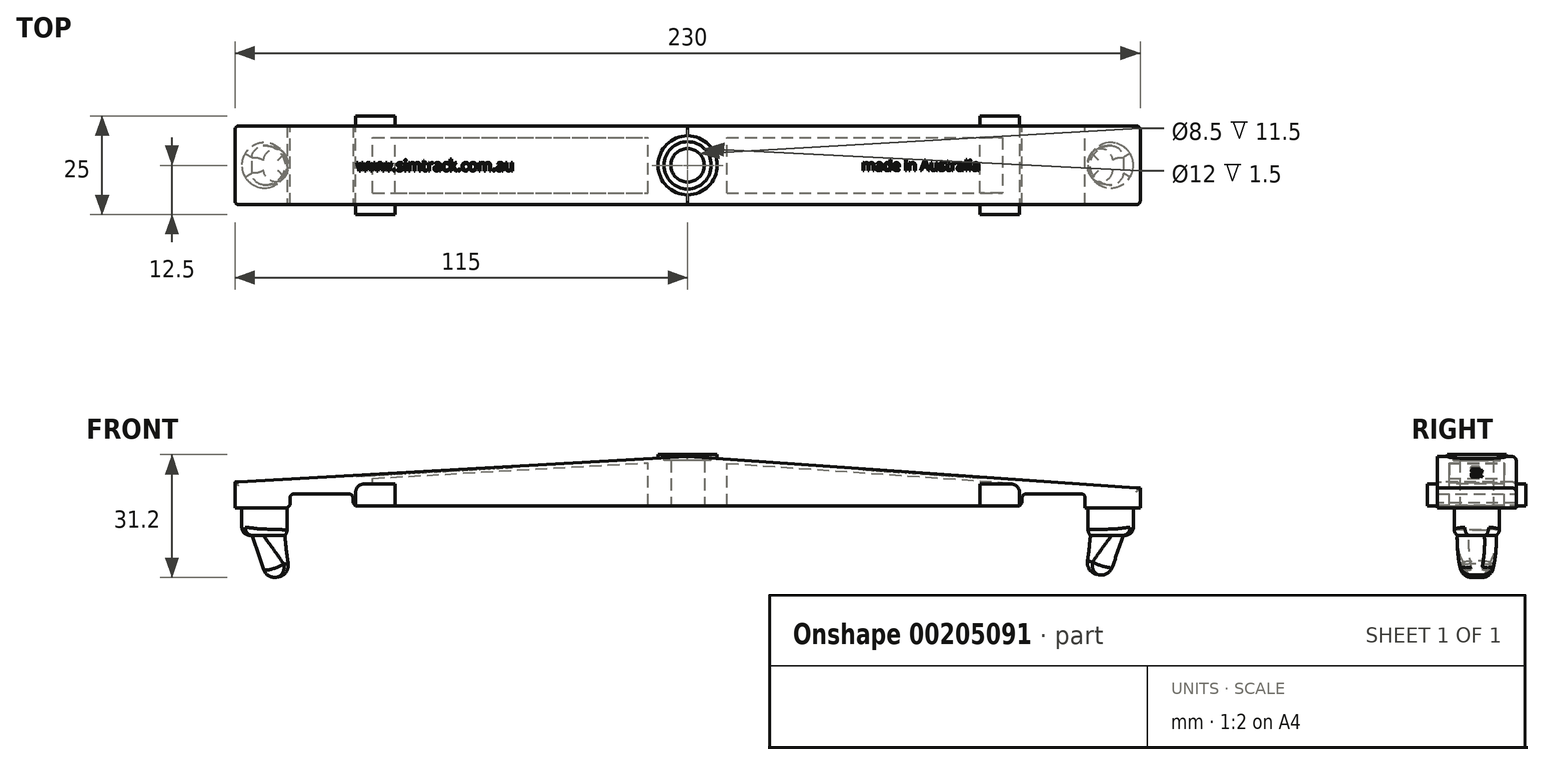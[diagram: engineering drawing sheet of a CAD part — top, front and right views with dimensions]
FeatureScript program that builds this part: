
annotation { "Feature Type Name" : "Feature", "Feature Type Description" : "" }
export const myFeature = defineFeature(function(context is Context, id is Id, definition is map)
    precondition{}
    {
        {
            var Q0;
            Q0=qCreatedBy(makeId("Top.planeOp"),FACE);
            var sketch = newSketch(context, id + "F0", { "sketchPlane" : qUnion([Q0])});
            skCircle(sketch, "E0", {"center": v(0, 0) * mm, "radius": 4.25 * mm});
            skLineSegment(sketch, "E1.bottom", {"start": v(115, -10) * mm, "end": v(-115, -10) * mm});
            skLineSegment(sketch, "E1.top", {"start": v(115, 10) * mm, "end": v(-115, 10) * mm});
            skLineSegment(sketch, "E1.left", {"start": v(115, -10) * mm, "end": v(115, 10) * mm});
            skLineSegment(sketch, "E1.right", {"start": v(-115, -10) * mm, "end": v(-115, 10) * mm});
            skPoint(sketch, "E2.visualSharp", {"position": v(-115, 10) * mm});
            skLineSegment(sketch, "E2.filletArc", {"start": v(-115, 10) * mm, "end": v(-115, 10) * mm});
            skPoint(sketch, "E3.visualSharp", {"position": v(-115, -10) * mm});
            skLineSegment(sketch, "E3.filletArc", {"start": v(-115, -10) * mm, "end": v(-115, -10) * mm});
            skPoint(sketch, "E4.visualSharp", {"position": v(115, 10) * mm});
            skLineSegment(sketch, "E4.filletArc", {"start": v(115, 10) * mm, "end": v(115, 10) * mm});
            skPoint(sketch, "E5.visualSharp", {"position": v(115, -10) * mm});
            skLineSegment(sketch, "E5.filletArc", {"start": v(115, -10) * mm, "end": v(115, -10) * mm});
            skLineSegment(sketch, "E6.bottom", {"start": v(80, 7) * mm, "end": v(10, 7) * mm});
            skLineSegment(sketch, "E6.top", {"start": v(80, -7) * mm, "end": v(10, -7) * mm});
            skLineSegment(sketch, "E6.left", {"start": v(80, 7) * mm, "end": v(80, -7) * mm});
            skLineSegment(sketch, "E6.right", {"start": v(10, 7) * mm, "end": v(10, -7) * mm});
            skLineSegment(sketch, "E7.bottom", {"start": v(-10, 7) * mm, "end": v(-80, 7) * mm});
            skLineSegment(sketch, "E7.top", {"start": v(-10, -7) * mm, "end": v(-80, -7) * mm});
            skLineSegment(sketch, "E7.left", {"start": v(-10, 7) * mm, "end": v(-10, -7) * mm});
            skLineSegment(sketch, "E7.right", {"start": v(-80, 7) * mm, "end": v(-80, -7) * mm});
            skCircle(sketch, "E8", {"center": v(0, 0) * mm, "radius": 7.5 * mm});
            skSolve(sketch);
        }
        {
            var Q0;
            Q0=makeQuery(id+"F0.imprint","IMPRINT",FACE,{"disambiguationData":[TD([[makeQuery(id+"F0.imprint","IMPRINT",EDGE,{"derivedFrom":sQuery(id+"F0.wireOp",EDGE,"E1.bottom")}),-1.0]])]});
            var Q1;
            Q1=makeQuery(id+"F0.imprint","IMPRINT",FACE,{"disambiguationData":[TD([[makeQuery(id+"F0.imprint","IMPRINT",EDGE,{"derivedFrom":sQuery(id+"F0.wireOp",EDGE,"q9BRd2um-oMs7-7MK2-WjCr-aT8UQEt5jsp8")}),-1.0]])]});
            var Q2;
            {var subQ0=sQuery(id+"F0.wireOp",EDGE,"CfEYtvD2-7vdv-HU4w-jJwD-IvnwvT9jjSvh.right");var subQ1=sQuery(id+"F0.wireOp",EDGE,"TnjMtal5-3gMc-DNrO-T4Mg-M14iXYZFMKTD");var subQ2=makeQuery(id+"F0.imprint","INTERSECT",VERTEX,{"disambiguationData":[OD(0.0)],"derivedFrom":[subQ1,subQ0]});Q2=makeQuery(id+"F0.imprint","IMPRINT",FACE,{"disambiguationData":[TD([[makeQuery(id+"F0.imprint","IMPRINT",EDGE,{"disambiguationData":[TD([[subQ2,1.0]])],"derivedFrom":subQ1}),1.0]])]});}
            var Q3;
            {var subQ0=sQuery(id+"F0.wireOp",EDGE,"CfEYtvD2-7vdv-HU4w-jJwD-IvnwvT9jjSvh.left");var subQ1=sQuery(id+"F0.wireOp",EDGE,"O0jPoW7s-RU5z-iA6U-w5ju-wIfl1B3ZVbkh");var subQ2=makeQuery(id+"F0.imprint","INTERSECT",VERTEX,{"disambiguationData":[OD(0.0)],"derivedFrom":[subQ1,subQ0]});Q3=makeQuery(id+"F0.imprint","IMPRINT",FACE,{"disambiguationData":[TD([[makeQuery(id+"F0.imprint","IMPRINT",EDGE,{"disambiguationData":[TD([[subQ2,-1.0]])],"derivedFrom":subQ1}),1.0]])]});}
            var Q4;
            {var subQ0=sQuery(id+"F0.wireOp",EDGE,"CfEYtvD2-7vdv-HU4w-jJwD-IvnwvT9jjSvh.right");var subQ1=sQuery(id+"F0.wireOp",EDGE,"TnjMtal5-3gMc-DNrO-T4Mg-M14iXYZFMKTD");var subQ2=makeQuery(id+"F0.imprint","INTERSECT",VERTEX,{"disambiguationData":[OD(0.0)],"derivedFrom":[subQ1,subQ0]});Q4=makeQuery(id+"F0.imprint","IMPRINT",FACE,{"disambiguationData":[TD([[makeQuery(id+"F0.imprint","IMPRINT",EDGE,{"disambiguationData":[TD([[subQ2,-1.0]])],"derivedFrom":subQ1}),1.0]])]});}
            var Q5;
            {var subQ0=sQuery(id+"F0.wireOp",EDGE,"CfEYtvD2-7vdv-HU4w-jJwD-IvnwvT9jjSvh.left");var subQ1=sQuery(id+"F0.wireOp",EDGE,"O0jPoW7s-RU5z-iA6U-w5ju-wIfl1B3ZVbkh");var subQ2=makeQuery(id+"F0.imprint","INTERSECT",VERTEX,{"disambiguationData":[OD(0.0)],"derivedFrom":[subQ1,subQ0]});Q5=makeQuery(id+"F0.imprint","IMPRINT",FACE,{"disambiguationData":[TD([[makeQuery(id+"F0.imprint","IMPRINT",EDGE,{"disambiguationData":[TD([[subQ2,1.0]])],"derivedFrom":subQ1}),1.0]])]});}
            extrude(context, id + "F1", {"entities" : qUnion([Q0, Q1, Q2, Q3, Q4, Q5]), "oppositeDirection" : true, "depth" : 5 * mm, "hasSecondDirection" : true, "secondDirectionOppositeDirection" : false, "secondDirectionDepth" : 8 * mm});
        }
        {
            var Q0;
            Q0=makeQuery(id+"F1.opExtrude","SWEPT_FACE",FACE,{"disambiguationData":[OSD([sQuery(id+"F0.wireOp",EDGE,"E1.bottom")])]});
            var sketch = newSketch(context, id + "F2", { "sketchPlane" : qUnion([Q0])});
            skLineSegment(sketch, "E9", {"start": v(-115, 1.5) * mm, "end": v(0, 8) * mm});
            skLineSegment(sketch, "E10", {"start": v(0, 8) * mm, "end": v(115, 0) * mm});
            skSolve(sketch);
        }
        {
            var Q0;
            {var subQ0=sQuery(id+"F2.wireOp",EDGE,"E10");Q0=makeQuery(id+"F2.imprint","IMPRINT",FACE,{"disambiguationData":[TD([[makeQuery(id+"F2.imprint","IMPRINT",EDGE,{"derivedFrom":subQ0}),1.0]])]});}
            var Q1;
            {var subQ0=sQuery(id+"F2.wireOp",EDGE,"E9");Q1=makeQuery(id+"F2.imprint","IMPRINT",FACE,{"disambiguationData":[TD([[makeQuery(id+"F2.imprint","IMPRINT",EDGE,{"derivedFrom":subQ0}),1.0]])]});}
            extrude(context, id + "F3", {"entities" : qUnion([Q0, Q1]), "operationType" : NewBodyOperationType.REMOVE, "oppositeDirection" : true, "depth" : 25 * mm});
        }
        {
            var Q0;
            Q0=makeQuery(id+"F0.imprint","IMPRINT",FACE,{"disambiguationData":[TD([[makeQuery(id+"F0.imprint","IMPRINT",EDGE,{"derivedFrom":sQuery(id+"F0.wireOp",EDGE,"E0")}),-1.0]])]});
            var Q1;
            Q1=makeQuery(id+"F0.imprint","IMPRINT",FACE,{"disambiguationData":[TD([[makeQuery(id+"F0.imprint","IMPRINT",EDGE,{"derivedFrom":sQuery(id+"F0.wireOp",EDGE,"E0")}),1.0]])]});
            extrude(context, id + "F4", {"entities" : qUnion([Q0, Q1]), "operationType" : NewBodyOperationType.ADD, "oppositeDirection" : true, "depth" : 5 * mm});
        }
        {
            var Q0;
            Q0=makeQuery(id+"F0.imprint","IMPRINT",FACE,{"disambiguationData":[TD([[makeQuery(id+"F0.imprint","IMPRINT",EDGE,{"derivedFrom":sQuery(id+"F0.wireOp",EDGE,"E0")}),1.0]])]});
            extrude(context, id + "F5", {"entities" : qUnion([Q0]), "operationType" : NewBodyOperationType.REMOVE, "depth" : 8 * mm, "hasSecondDirection" : true, "secondDirectionOppositeDirection" : true, "secondDirectionDepth" : 5 * mm});
        }
        {
            var Q0;
            Q0=makeQuery(id+"F1.opExtrude","SWEPT_FACE",FACE,{"disambiguationData":[OSD([sQuery(id+"F0.wireOp",EDGE,"E1.bottom")])]});
            var sketch = newSketch(context, id + "F6", { "sketchPlane" : qUnion([Q0])});
            skSolve(sketch);
        }
        {
            var Q0;
            Q0=makeQuery(id+"F1.opExtrude","SWEPT_FACE",FACE,{"disambiguationData":[OSD([sQuery(id+"F0.wireOp",EDGE,"E1.top")])]});
            var sketch = newSketch(context, id + "F7", { "sketchPlane" : qUnion([Q0])});
            skLineSegment(sketch, "E11", {"start": v(-115, -5) * mm, "end": v(-101, -5) * mm});
            skLineSegment(sketch, "E12", {"start": v(-101, -5) * mm, "end": v(-101, -1.5) * mm});
            skLineSegment(sketch, "E13", {"start": v(-101, -1.5) * mm, "end": v(-85, -1.5) * mm});
            skLineSegment(sketch, "E14", {"start": v(-85, -1.5) * mm, "end": v(-85, -5) * mm});
            skLineSegment(sketch, "E15", {"start": v(-85, -5) * mm, "end": v(-101, -5) * mm});
            skLineSegment(sketch, "E16", {"start": v(115, -5) * mm, "end": v(101, -5) * mm});
            skLineSegment(sketch, "E17", {"start": v(101, -5) * mm, "end": v(101, -1.5) * mm});
            skLineSegment(sketch, "E18", {"start": v(101, -1.5) * mm, "end": v(85, -1.5) * mm});
            skLineSegment(sketch, "E19", {"start": v(85, -1.5) * mm, "end": v(85, -5) * mm});
            skLineSegment(sketch, "E20", {"start": v(85, -5) * mm, "end": v(101, -5) * mm});
            skSolve(sketch);
        }
        {
            var Q0;
            Q0=makeQuery(id+"F7.imprint","IMPRINT",FACE,{"disambiguationData":[TD([[makeQuery(id+"F7.imprint","IMPRINT",EDGE,{"derivedFrom":sQuery(id+"F7.wireOp",EDGE,"E12")}),-1.0]])]});
            var Q1;
            Q1=makeQuery(id+"F7.imprint","IMPRINT",FACE,{"disambiguationData":[TD([[makeQuery(id+"F7.imprint","IMPRINT",EDGE,{"derivedFrom":sQuery(id+"F7.wireOp",EDGE,"E17")}),1.0]])]});
            extrude(context, id + "F8", {"entities" : qUnion([Q0, Q1]), "operationType" : NewBodyOperationType.REMOVE, "oppositeDirection" : true, "depth" : 25 * mm});
        }
        {
            var Q0;
            Q0=makeQuery(id+"F3.boolean.opBoolean","COPY",FACE,{"derivedFrom":makeQuery(id+"F3.opExtrude","SWEPT_FACE",FACE,{"disambiguationData":[OSD([sQuery(id+"F2.wireOp",EDGE,"E9")])]})});
            var sketch = newSketch(context, id + "F9", { "sketchPlane" : qUnion([Q0])});
            skCircle(sketch, "E21", {"center": v(-107.72, 0) * mm, "radius": 5 * mm});
            skSolve(sketch);
        }
        {
            var Q0;
            Q0=makeQuery(id+"F9.imprint","IMPRINT",FACE,{"disambiguationData":[TD([[makeQuery(id+"F9.imprint","IMPRINT",EDGE,{"derivedFrom":sQuery(id+"F9.wireOp",EDGE,"E21")}),1.0]])]});
            extrude(context, id + "F10", {"entities" : qUnion([Q0]), "operationType" : NewBodyOperationType.ADD, "oppositeDirection" : true, "depth" : 8 * mm});
        }
        {
            var Q0;
            Q0=makeQuery(id+"F3.boolean.opBoolean","COPY",FACE,{"derivedFrom":makeQuery(id+"F3.opExtrude","SWEPT_FACE",FACE,{"disambiguationData":[OSD([sQuery(id+"F2.wireOp",EDGE,"E10")])]})});
            var sketch = newSketch(context, id + "F11", { "sketchPlane" : qUnion([Q0])});
            skCircle(sketch, "E22", {"center": v(107.7, 0) * mm, "radius": 5 * mm});
            skSolve(sketch);
        }
        {
            var Q0;
            Q0=makeQuery(id+"F11.imprint","IMPRINT",FACE,{"disambiguationData":[TD([[makeQuery(id+"F11.imprint","IMPRINT",EDGE,{"derivedFrom":sQuery(id+"F11.wireOp",EDGE,"E22")}),1.0]])]});
            extrude(context, id + "F12", {"entities" : qUnion([Q0]), "operationType" : NewBodyOperationType.ADD, "oppositeDirection" : true, "depth" : 6 * mm});
        }
        {
            var Q0;
            Q0=makeQuery(id+"F0.imprint","IMPRINT",FACE,{"disambiguationData":[TD([[makeQuery(id+"F0.imprint","IMPRINT",EDGE,{"derivedFrom":sQuery(id+"F0.wireOp",EDGE,"E7.bottom")}),1.0]])]});
            var Q1;
            Q1=makeQuery(id+"F0.imprint","IMPRINT",FACE,{"disambiguationData":[TD([[makeQuery(id+"F0.imprint","IMPRINT",EDGE,{"derivedFrom":sQuery(id+"F0.wireOp",EDGE,"E6.bottom")}),1.0]])]});
            extrude(context, id + "F13", {"entities" : qUnion([Q0, Q1]), "operationType" : NewBodyOperationType.REMOVE, "depth" : 29 * mm, "hasDraft" : true, "draftAngle" : 3 * degree});
        }
        {
            var Q0;
            {var subQ0=sQuery(id+"F0.wireOp",EDGE,"E1.bottom");Q0=makeQuery(id+"F6.imprint","IMPRINT",FACE,{"disambiguationData":[TD([[makeQuery(id+"F6.imprint","IMPRINT",EDGE,{"derivedFrom":makeQuery(id+"F1.opExtrude","CAP_EDGE",EDGE,{"disambiguationData":[OSD([subQ0])],"isStart":false})}),-1.0]])]});}
            var sketch = newSketch(context, id + "F14", { "sketchPlane" : qUnion([Q0])});
            skSolve(sketch);
        }
        {
            var Q0;
            Q0=makeQuery(id+"F1.opExtrude","SWEPT_FACE",FACE,{"disambiguationData":[OSD([sQuery(id+"F0.wireOp",EDGE,"E1.top")])]});
            extrude(context, id + "F15", {"entities" : qUnion([Q0]), "operationType" : NewBodyOperationType.ADD, "oppositeDirection" : true, "depth" : 20 * mm});
        }
        {
            var Q0;
            Q0=makeQuery(id+"F0.imprint","IMPRINT",FACE,{"disambiguationData":[TD([[makeQuery(id+"F0.imprint","IMPRINT",EDGE,{"derivedFrom":sQuery(id+"F0.wireOp",EDGE,"E7.bottom")}),1.0]])]});
            var Q1;
            Q1=makeQuery(id+"F0.imprint","IMPRINT",FACE,{"disambiguationData":[TD([[makeQuery(id+"F0.imprint","IMPRINT",EDGE,{"derivedFrom":sQuery(id+"F0.wireOp",EDGE,"E6.bottom")}),1.0]])]});
            extrude(context, id + "F16", {"entities" : qUnion([Q0, Q1]), "operationType" : NewBodyOperationType.REMOVE, "oppositeDirection" : true, "depth" : 25 * mm, "hasSecondDirection" : true, "secondDirectionOppositeDirection" : false, "secondDirectionDepth" : 25 * mm});
        }
        {
            var Q0;
            Q0=makeQuery(id+"F0.imprint","IMPRINT",FACE,{"disambiguationData":[TD([[makeQuery(id+"F0.imprint","IMPRINT",EDGE,{"derivedFrom":sQuery(id+"F0.wireOp",EDGE,"E0")}),-1.0]])]});
            extrude(context, id + "F17", {"entities" : qUnion([Q0]), "operationType" : NewBodyOperationType.ADD, "depth" : 8.5 * mm});
        }
        {
            var Q0;
            Q0=makeQuery(id+"F0.imprint","IMPRINT",FACE,{"disambiguationData":[TD([[makeQuery(id+"F0.imprint","IMPRINT",EDGE,{"derivedFrom":sQuery(id+"F0.wireOp",EDGE,"E0")}),1.0]])]});
            extrude(context, id + "F18", {"entities" : qUnion([Q0]), "operationType" : NewBodyOperationType.REMOVE, "oppositeDirection" : true, "depth" : 25 * mm, "hasSecondDirection" : true, "secondDirectionOppositeDirection" : false, "secondDirectionDepth" : 25 * mm});
        }
        {
            var Q0;
            Q0=makeQuery(id+"F3.boolean.opBoolean","COPY",EDGE,{"derivedFrom":makeQuery(id+"F3.opExtrude","SWEPT_EDGE",EDGE,{"disambiguationData":[OSD([sQuery(id+"F0.wireOp",EDGE,"E1.bottom"),sQuery(id+"F0.wireOp",EDGE,"E1.left"),sQuery(id+"F2.wireOp",EDGE,"E10")])]})});
            var Q1;
            Q1=makeQuery(id+"F3.boolean.opBoolean","INTERSECT",EDGE,{"derivedFrom":[makeQuery(id+"F1.opExtrude","SWEPT_FACE",FACE,{"disambiguationData":[OSD([sQuery(id+"F0.wireOp",EDGE,"E1.top")])]}),makeQuery(id+"F3.opExtrude","SWEPT_FACE",FACE,{"disambiguationData":[OSD([sQuery(id+"F2.wireOp",EDGE,"E10")])]})]});
            var Q2;
            Q2=makeQuery(id+"F3.boolean.opBoolean","INTERSECT",EDGE,{"derivedFrom":[makeQuery(id+"F1.opExtrude","SWEPT_FACE",FACE,{"disambiguationData":[OSD([sQuery(id+"F0.wireOp",EDGE,"E1.top")])]}),makeQuery(id+"F3.opExtrude","SWEPT_FACE",FACE,{"disambiguationData":[OSD([sQuery(id+"F2.wireOp",EDGE,"E9")])]})]});
            var Q3;
            Q3=makeQuery(id+"F3.boolean.opBoolean","COPY",EDGE,{"derivedFrom":makeQuery(id+"F3.opExtrude","SWEPT_EDGE",EDGE,{"disambiguationData":[OSD([sQuery(id+"F0.wireOp",EDGE,"E1.bottom"),sQuery(id+"F0.wireOp",EDGE,"E1.right"),sQuery(id+"F2.wireOp",EDGE,"E9")])]})});
            var Q4;
            Q4=makeQuery(id+"F1.opExtrude","SWEPT_EDGE",EDGE,{"disambiguationData":[OSD([sQuery(id+"F0.wireOp",EDGE,"E1.bottom"),sQuery(id+"F0.wireOp",EDGE,"E1.right")])]});
            var Q5;
            Q5=makeQuery(id+"F1.opExtrude","SWEPT_EDGE",EDGE,{"disambiguationData":[OSD([sQuery(id+"F0.wireOp",EDGE,"E1.top"),sQuery(id+"F0.wireOp",EDGE,"E1.right")])]});
            var Q6;
            Q6=makeQuery(id+"F3.boolean.opBoolean","COPY",EDGE,{"derivedFrom":makeQuery(id+"F3.opExtrude","CAP_EDGE",EDGE,{"disambiguationData":[OSD([sQuery(id+"F2.wireOp",EDGE,"E10")])],"isStart":true})});
            var Q7;
            Q7=makeQuery(id+"F3.boolean.opBoolean","COPY",EDGE,{"derivedFrom":makeQuery(id+"F3.opExtrude","CAP_EDGE",EDGE,{"disambiguationData":[OSD([sQuery(id+"F2.wireOp",EDGE,"E9")])],"isStart":true})});
            var Q8;
            Q8=makeQuery(id+"F1.opExtrude","SWEPT_EDGE",EDGE,{"disambiguationData":[OSD([sQuery(id+"F0.wireOp",EDGE,"E1.top"),sQuery(id+"F0.wireOp",EDGE,"E1.left")])]});
            var Q9;
            Q9=makeQuery(id+"F1.opExtrude","SWEPT_EDGE",EDGE,{"disambiguationData":[OSD([sQuery(id+"F0.wireOp",EDGE,"E1.bottom"),sQuery(id+"F0.wireOp",EDGE,"E1.left")])]});
            fillet(context, id + "F19", {"entities" : qUnion([Q0, Q1, Q2, Q3, Q4, Q5, Q6, Q7, Q8, Q9]), "radius" : 1 * mm, "tangentPropagation" : true, "allowEdgeOverflow" : false});
        }
        {
            var Q0;
            Q0=makeQuery(id+"F8.boolean.opBoolean","COPY",EDGE,{"derivedFrom":makeQuery(id+"F8.opExtrude","SWEPT_EDGE",EDGE,{"disambiguationData":[OSD([sQuery(id+"F7.wireOp",EDGE,"E18"),sQuery(id+"F7.wireOp",EDGE,"E19")])]})});
            var Q1;
            Q1=makeQuery(id+"F8.boolean.opBoolean","COPY",EDGE,{"derivedFrom":makeQuery(id+"F8.opExtrude","SWEPT_EDGE",EDGE,{"disambiguationData":[OSD([sQuery(id+"F7.wireOp",EDGE,"E17"),sQuery(id+"F7.wireOp",EDGE,"E18")])]})});
            var Q2;
            Q2=makeQuery(id+"F8.boolean.opBoolean","COPY",EDGE,{"derivedFrom":makeQuery(id+"F8.opExtrude","SWEPT_EDGE",EDGE,{"disambiguationData":[OSD([sQuery(id+"F7.wireOp",EDGE,"E13"),sQuery(id+"F7.wireOp",EDGE,"E14")])]})});
            var Q3;
            Q3=makeQuery(id+"F8.boolean.opBoolean","COPY",EDGE,{"derivedFrom":makeQuery(id+"F8.opExtrude","SWEPT_EDGE",EDGE,{"disambiguationData":[OSD([sQuery(id+"F7.wireOp",EDGE,"E12"),sQuery(id+"F7.wireOp",EDGE,"E13")])]})});
            fillet(context, id + "F20", {"entities" : qUnion([Q0, Q1, Q2, Q3]), "radius" : 1 * mm, "tangentPropagation" : true, "allowEdgeOverflow" : false});
        }
        {
            var Q0;
            {var subQ1=sQuery(id+"F0.wireOp",EDGE,"E1.top");var subQ2=sQuery(id+"F2.wireOp",EDGE,"E10");Q0=makeQuery(id+"F17.boolean.opBoolean","SPLIT",FACE,{"disambiguationData":[TD([makeQuery(id+"F1.opExtrude","SWEPT_FACE",FACE,{"disambiguationData":[OSD([sQuery(id+"F0.wireOp",EDGE,"E1.bottom")])]})])],"derivedFrom":makeQuery(id+"F15.boolean.opBoolean","MERGE",FACE,{"derivedFrom":[makeQuery(id+"F3.boolean.opBoolean","COPY",FACE,{"derivedFrom":makeQuery(id+"F3.opExtrude","SWEPT_FACE",FACE,{"disambiguationData":[OSD([subQ2])]})}),makeQuery(id+"F15.opExtrude","SWEPT_FACE",FACE,{"disambiguationData":[OSD([subQ1,subQ2])]})]})});}
            var sketch = newSketch(context, id + "F21", { "sketchPlane" : qUnion([Q0])});
            skSolve(sketch);
        }
        {
            var Q0;
            Q0=makeQuery(id+"F12.opExtrude","CAP_FACE",FACE,{"disambiguationData":[OSD([sQuery(id+"F0.wireOp",EDGE,"O0jPoW7s-RU5z-iA6U-w5ju-wIfl1B3ZVbkh"),sQuery(id+"F2.wireOp",EDGE,"E10"),sQuery(id+"F11.wireOp",EDGE,"E22")])],"isStart":false});
            var Q1;
            {var subQ0=sQuery(id+"F0.wireOp",EDGE,"E6.right");var subQ1=makeQuery(id+"F8.opExtrude","SWEPT_FACE",FACE,{"disambiguationData":[OSD([sQuery(id+"F7.wireOp",EDGE,"E14")])]});var subQ2=sQuery(id+"F0.wireOp",EDGE,"E1.top");var subQ4=sQuery(id+"F0.wireOp",EDGE,"E8");var subQ5=makeQuery(id+"F4.opExtrude","CAP_FACE",FACE,{"disambiguationData":[OSD([subQ4])],"isStart":false});var subQ6=sQuery(id+"F0.wireOp",EDGE,"E7.right");var subQ7=sQuery(id+"F0.wireOp",EDGE,"E7.left");var subQ8=sQuery(id+"F0.wireOp",EDGE,"E7.top");var subQ9=sQuery(id+"F0.wireOp",EDGE,"E7.bottom");var subQ10=sQuery(id+"F0.wireOp",EDGE,"E6.left");var subQ11=sQuery(id+"F0.wireOp",EDGE,"E6.top");var subQ12=sQuery(id+"F0.wireOp",EDGE,"E6.bottom");var subQ13=sQuery(id+"F0.wireOp",EDGE,"E1.bottom");var subQ14=makeQuery(id+"F1.opExtrude","CAP_FACE",FACE,{"disambiguationData":[OSD([sQuery(id+"F0.wireOp",EDGE,"O0jPoW7s-RU5z-iA6U-w5ju-wIfl1B3ZVbkh"),sQuery(id+"F0.wireOp",EDGE,"TnjMtal5-3gMc-DNrO-T4Mg-M14iXYZFMKTD"),subQ13,subQ2,sQuery(id+"F0.wireOp",EDGE,"E1.left"),sQuery(id+"F0.wireOp",EDGE,"E1.right"),subQ12,subQ11,subQ10,subQ0,subQ9,subQ8,subQ7,subQ6,subQ4])],"isStart":false});Q1=makeQuery(id+"F16.boolean.opBoolean","INTERSECT",EDGE,{"derivedFrom":[makeQuery(id+"F15.boolean.opBoolean","MERGE",FACE,{"derivedFrom":[makeQuery(id+"F8.boolean.opBoolean","SPLIT",FACE,{"disambiguationData":[TD([makeQuery(id+"F1.opExtrude","SWEPT_FACE",FACE,{"disambiguationData":[OSD([subQ12])]})])],"derivedFrom":makeQuery(id+"F4.boolean.opBoolean","MERGE",FACE,{"derivedFrom":[subQ14,subQ5]})}),makeQuery(id+"F15.opExtrude","SWEPT_FACE",FACE,{"disambiguationData":[OSD([subQ2]),TDD([makeQuery(id+"F8.boolean.opBoolean","SPLIT",EDGE,{"disambiguationData":[TD([subQ1])],"derivedFrom":makeQuery(id+"F1.opExtrude","CAP_EDGE",EDGE,{"disambiguationData":[OSD([subQ2])],"isStart":false})})])]})]}),makeQuery(id+"F16.opExtrude","SWEPT_FACE",FACE,{"disambiguationData":[OSD([subQ0])]})]});}
            revolve(context, id + "F22", {"operationType" : NewBodyOperationType.ADD, "entities" : qUnion([Q0]), "axis" : qUnion([Q1]), "revolveType" : RevolveType.ONE_DIRECTION, "oppositeDirection" : true, "angle" : 10 * degree});
        }
        {
            var Q0;
            Q0=makeQuery(id+"F10.opExtrude","CAP_FACE",FACE,{"disambiguationData":[OSD([sQuery(id+"F0.wireOp",EDGE,"TnjMtal5-3gMc-DNrO-T4Mg-M14iXYZFMKTD"),sQuery(id+"F2.wireOp",EDGE,"E9"),sQuery(id+"F9.wireOp",EDGE,"E21")])],"isStart":false});
            var Q1;
            {var subQ0=sQuery(id+"F0.wireOp",EDGE,"E7.left");var subQ1=makeQuery(id+"F8.opExtrude","SWEPT_FACE",FACE,{"disambiguationData":[OSD([sQuery(id+"F7.wireOp",EDGE,"E14")])]});var subQ2=sQuery(id+"F0.wireOp",EDGE,"E1.top");var subQ4=sQuery(id+"F0.wireOp",EDGE,"E8");var subQ5=makeQuery(id+"F4.opExtrude","CAP_FACE",FACE,{"disambiguationData":[OSD([subQ4])],"isStart":false});var subQ6=sQuery(id+"F0.wireOp",EDGE,"E7.right");var subQ7=sQuery(id+"F0.wireOp",EDGE,"E7.top");var subQ8=sQuery(id+"F0.wireOp",EDGE,"E7.bottom");var subQ9=sQuery(id+"F0.wireOp",EDGE,"E6.right");var subQ10=sQuery(id+"F0.wireOp",EDGE,"E6.left");var subQ11=sQuery(id+"F0.wireOp",EDGE,"E6.top");var subQ12=sQuery(id+"F0.wireOp",EDGE,"E6.bottom");var subQ13=sQuery(id+"F0.wireOp",EDGE,"E1.bottom");var subQ14=makeQuery(id+"F1.opExtrude","CAP_FACE",FACE,{"disambiguationData":[OSD([sQuery(id+"F0.wireOp",EDGE,"O0jPoW7s-RU5z-iA6U-w5ju-wIfl1B3ZVbkh"),sQuery(id+"F0.wireOp",EDGE,"TnjMtal5-3gMc-DNrO-T4Mg-M14iXYZFMKTD"),subQ13,subQ2,sQuery(id+"F0.wireOp",EDGE,"E1.left"),sQuery(id+"F0.wireOp",EDGE,"E1.right"),subQ12,subQ11,subQ10,subQ9,subQ8,subQ7,subQ0,subQ6,subQ4])],"isStart":false});Q1=makeQuery(id+"F16.boolean.opBoolean","INTERSECT",EDGE,{"derivedFrom":[makeQuery(id+"F15.boolean.opBoolean","MERGE",FACE,{"derivedFrom":[makeQuery(id+"F8.boolean.opBoolean","SPLIT",FACE,{"disambiguationData":[TD([makeQuery(id+"F1.opExtrude","SWEPT_FACE",FACE,{"disambiguationData":[OSD([subQ12])]})])],"derivedFrom":makeQuery(id+"F4.boolean.opBoolean","MERGE",FACE,{"derivedFrom":[subQ14,subQ5]})}),makeQuery(id+"F15.opExtrude","SWEPT_FACE",FACE,{"disambiguationData":[OSD([subQ2]),TDD([makeQuery(id+"F8.boolean.opBoolean","SPLIT",EDGE,{"disambiguationData":[TD([subQ1])],"derivedFrom":makeQuery(id+"F1.opExtrude","CAP_EDGE",EDGE,{"disambiguationData":[OSD([subQ2])],"isStart":false})})])]})]}),makeQuery(id+"F16.opExtrude","SWEPT_FACE",FACE,{"disambiguationData":[OSD([subQ0])]})]});}
            revolve(context, id + "F23", {"operationType" : NewBodyOperationType.ADD, "entities" : qUnion([Q0]), "axis" : qUnion([Q1]), "revolveType" : RevolveType.ONE_DIRECTION, "angle" : 10 * degree});
        }
        {
            var Q0;
            {var subQ0=sQuery(id+"F0.wireOp",EDGE,"E1.bottom");Q0=makeQuery(id+"F14.imprint","IMPRINT",FACE,{"disambiguationData":[TD([[makeQuery(id+"F14.imprint","IMPRINT",EDGE,{"derivedFrom":makeQuery(id+"F6.imprint","IMPRINT",EDGE,{"derivedFrom":makeQuery(id+"F1.opExtrude","CAP_EDGE",EDGE,{"disambiguationData":[OSD([subQ0])],"isStart":false})})}),-1.0]])]});}
            var sketch = newSketch(context, id + "F24", { "sketchPlane" : qUnion([Q0])});
            skLineSegment(sketch, "E23", {"start": v(-113, -5.27) * mm, "end": v(-105, -28.6) * mm});
            skLineSegment(sketch, "E24", {"start": v(-105, -28.6) * mm, "end": v(-114.46, -31.85) * mm});
            skLineSegment(sketch, "E25", {"start": v(-114.46, -31.85) * mm, "end": v(-123.26, -6.19) * mm});
            skLineSegment(sketch, "E26", {"start": v(-123.26, -6.19) * mm, "end": v(-113, -5.27) * mm});
            skLineSegment(sketch, "E27", {"start": v(-105, -28.6) * mm, "end": v(105, -28.6) * mm});
            skLineSegment(sketch, "E28", {"start": v(105, -28.6) * mm, "end": v(113, -5.27) * mm});
            skLineSegment(sketch, "E29", {"start": v(113, -5.27) * mm, "end": v(122.46, -8.5) * mm});
            skLineSegment(sketch, "E30", {"start": v(122.46, -8.5) * mm, "end": v(112.46, -37.7) * mm});
            skLineSegment(sketch, "E31", {"start": v(112.46, -37.7) * mm, "end": v(105, -28.6) * mm});
            skLineSegment(sketch, "E32", {"start": v(-136.8, -16.49) * mm, "end": v(163.26, -16.49) * mm});
            skPoint(sketch, "E33.orphan", {"position": v(-142.98, -6.19) * mm});
            skSolve(sketch);
        }
        {
            var Q0;
            Q0=makeQuery(id+"F24.imprint","IMPRINT",FACE,{"disambiguationData":[TD([[makeQuery(id+"F24.imprint","IMPRINT",EDGE,{"derivedFrom":sQuery(id+"F24.wireOp",EDGE,"E23")}),-1.0]])]});
            var Q1;
            Q1=makeQuery(id+"F24.imprint","IMPRINT",FACE,{"disambiguationData":[TD([[makeQuery(id+"F24.imprint","IMPRINT",EDGE,{"derivedFrom":sQuery(id+"F24.wireOp",EDGE,"E28")}),-1.0]])]});
            extrude(context, id + "F25", {"entities" : qUnion([Q0, Q1]), "operationType" : NewBodyOperationType.REMOVE, "oppositeDirection" : true, "depth" : 25 * mm});
        }
        {
            var Q0;
            {var subQ0=sQuery(id+"F0.wireOp",EDGE,"E1.bottom");Q0=makeQuery(id+"F14.imprint","IMPRINT",FACE,{"disambiguationData":[TD([[makeQuery(id+"F14.imprint","IMPRINT",EDGE,{"derivedFrom":makeQuery(id+"F6.imprint","IMPRINT",EDGE,{"derivedFrom":makeQuery(id+"F1.opExtrude","CAP_EDGE",EDGE,{"disambiguationData":[OSD([subQ0])],"isStart":false})})}),-1.0]])]});}
            var sketch = newSketch(context, id + "F26", { "sketchPlane" : qUnion([Q0])});
            skLineSegment(sketch, "E34.bottom", {"start": v(85.5, -8.11) * mm, "end": v(-85.5, -8.11) * mm});
            skLineSegment(sketch, "E34.top", {"start": v(85.5, -4.5) * mm, "end": v(-85.5, -4.5) * mm});
            skLineSegment(sketch, "E34.left", {"start": v(85.5, -8.11) * mm, "end": v(85.5, -4.5) * mm});
            skLineSegment(sketch, "E34.right", {"start": v(-85.5, -8.11) * mm, "end": v(-85.5, -4.5) * mm});
            skPoint(sketch, "E34.middle", {"position": v(0, -6.3) * mm});
            skSolve(sketch);
        }
        {
            var Q0;
            {var subQ0=sQuery(id+"F26.wireOp",EDGE,"E34.top");Q0=makeQuery(id+"F26.imprint","IMPRINT",FACE,{"disambiguationData":[TD([[makeQuery(id+"F26.imprint","IMPRINT",EDGE,{"derivedFrom":subQ0}),1.0]])]});}
            extrude(context, id + "F27", {"entities" : qUnion([Q0]), "operationType" : NewBodyOperationType.REMOVE, "oppositeDirection" : true, "depth" : 25 * mm});
        }
        {
            var Q0;
            Q0=makeQuery(id+"F25.boolean.opBoolean","INTERSECT",EDGE,{"derivedFrom":[makeQuery(id+"F23.opRevolve","SWEPT_FACE",FACE,{"disambiguationData":[OSD([sQuery(id+"F9.wireOp",EDGE,"E21")])]}),makeQuery(id+"F25.opExtrude","SWEPT_FACE",FACE,{"disambiguationData":[OSD([sQuery(id+"F24.wireOp",EDGE,"E23")])]})]});
            var Q1;
            Q1=makeQuery(id+"F23.opRevolve","CAP_EDGE",EDGE,{"disambiguationData":[OSD([sQuery(id+"F9.wireOp",EDGE,"E21")]),OD(1.0)],"isStart":false});
            var Q2;
            Q2=makeQuery(id+"F25.boolean.opBoolean","INTERSECT",EDGE,{"disambiguationData":[OD(1.0)],"derivedFrom":[makeQuery(id+"F23.opRevolve","CAP_FACE",FACE,{"disambiguationData":[OSD([sQuery(id+"F0.wireOp",EDGE,"TnjMtal5-3gMc-DNrO-T4Mg-M14iXYZFMKTD"),sQuery(id+"F2.wireOp",EDGE,"E9"),sQuery(id+"F9.wireOp",EDGE,"E21")])],"isStart":false}),makeQuery(id+"F25.opExtrude","SWEPT_FACE",FACE,{"disambiguationData":[OSD([sQuery(id+"F24.wireOp",EDGE,"E23")])]})]});
            var Q3;
            Q3=makeQuery(id+"F25.boolean.opBoolean","INTERSECT",EDGE,{"disambiguationData":[OD(0.0)],"derivedFrom":[makeQuery(id+"F23.opRevolve","CAP_FACE",FACE,{"disambiguationData":[OSD([sQuery(id+"F0.wireOp",EDGE,"TnjMtal5-3gMc-DNrO-T4Mg-M14iXYZFMKTD"),sQuery(id+"F2.wireOp",EDGE,"E9"),sQuery(id+"F9.wireOp",EDGE,"E21")])],"isStart":false}),makeQuery(id+"F25.opExtrude","SWEPT_FACE",FACE,{"disambiguationData":[OSD([sQuery(id+"F24.wireOp",EDGE,"E23")])]})]});
            var Q4;
            Q4=makeQuery(id+"F22.opRevolve","CAP_EDGE",EDGE,{"disambiguationData":[OSD([sQuery(id+"F11.wireOp",EDGE,"E22")]),OD(1.0)],"isStart":false});
            var Q5;
            Q5=makeQuery(id+"F25.boolean.opBoolean","INTERSECT",EDGE,{"derivedFrom":[makeQuery(id+"F22.opRevolve","SWEPT_FACE",FACE,{"disambiguationData":[OSD([sQuery(id+"F11.wireOp",EDGE,"E22")])]}),makeQuery(id+"F25.opExtrude","SWEPT_FACE",FACE,{"disambiguationData":[OSD([sQuery(id+"F24.wireOp",EDGE,"E28")])]})]});
            var Q6;
            Q6=makeQuery(id+"F25.boolean.opBoolean","INTERSECT",EDGE,{"disambiguationData":[OD(1.0)],"derivedFrom":[makeQuery(id+"F22.opRevolve","CAP_FACE",FACE,{"disambiguationData":[OSD([sQuery(id+"F0.wireOp",EDGE,"O0jPoW7s-RU5z-iA6U-w5ju-wIfl1B3ZVbkh"),sQuery(id+"F2.wireOp",EDGE,"E10"),sQuery(id+"F11.wireOp",EDGE,"E22")])],"isStart":false}),makeQuery(id+"F25.opExtrude","SWEPT_FACE",FACE,{"disambiguationData":[OSD([sQuery(id+"F24.wireOp",EDGE,"E28")])]})]});
            var Q7;
            Q7=makeQuery(id+"F25.boolean.opBoolean","INTERSECT",EDGE,{"disambiguationData":[OD(0.0)],"derivedFrom":[makeQuery(id+"F22.opRevolve","CAP_FACE",FACE,{"disambiguationData":[OSD([sQuery(id+"F0.wireOp",EDGE,"O0jPoW7s-RU5z-iA6U-w5ju-wIfl1B3ZVbkh"),sQuery(id+"F2.wireOp",EDGE,"E10"),sQuery(id+"F11.wireOp",EDGE,"E22")])],"isStart":false}),makeQuery(id+"F25.opExtrude","SWEPT_FACE",FACE,{"disambiguationData":[OSD([sQuery(id+"F24.wireOp",EDGE,"E28")])]})]});
            fillet(context, id + "F28", {"entities" : qUnion([Q0, Q1, Q2, Q3, Q4, Q5, Q6, Q7]), "radius" : 3 * mm, "allowEdgeOverflow" : false});
        }
        {
            var Q0;
            Q0=qCreatedBy(makeId("Top.planeOp"),FACE);
            var sketch = newSketch(context, id + "F29", { "sketchPlane" : qUnion([Q0])});
            skLineSegment(sketch, "E35", {"start": v(-136.77, 0) * mm, "end": v(141.95, 0) * mm});
            skCircle(sketch, "E36", {"center": v(107.5, 0) * mm, "radius": 5.75 * mm});
            skCircle(sketch, "E37", {"center": v(-107.5, 0) * mm, "radius": 5.75 * mm});
            skCircle(sketch, "E38", {"center": v(-107.5, 0) * mm, "radius": 2.5 * mm});
            skCircle(sketch, "E39", {"center": v(107.5, 0) * mm, "radius": 2.5 * mm});
            skSolve(sketch);
        }
        {
            var Q0;
            Q0 = qSketchRegion(id + "F29", true);
            extrude(context, id + "F30", {"entities" : qUnion([Q0]), "operationType" : NewBodyOperationType.ADD, "oppositeDirection" : true, "depth" : 12 * mm});
        }
        {
            var Q0;
            Q0=makeQuery(id+"F30.opExtrude","CAP_EDGE",EDGE,{"disambiguationData":[OSD([sQuery(id+"F29.wireOp",EDGE,"E37")])],"isStart":false});
            var Q1;
            Q1=makeQuery(id+"F30.opExtrude","CAP_EDGE",EDGE,{"disambiguationData":[OSD([sQuery(id+"F29.wireOp",EDGE,"E36")])],"isStart":false});
            fillet(context, id + "F31", {"entities" : qUnion([Q0, Q1]), "radius" : 2 * mm, "tangentPropagation" : true, "allowEdgeOverflow" : false});
        }
        {
            var Q0;
            {var subQ0=sQuery(id+"F0.wireOp",EDGE,"E1.top");var subQ2=sQuery(id+"F2.wireOp",EDGE,"E9");Q0=makeQuery(id+"F17.boolean.opBoolean","SPLIT",FACE,{"disambiguationData":[TD([makeQuery(id+"F1.opExtrude","SWEPT_FACE",FACE,{"disambiguationData":[OSD([sQuery(id+"F0.wireOp",EDGE,"E1.bottom")])]})])],"derivedFrom":makeQuery(id+"F15.boolean.opBoolean","MERGE",FACE,{"derivedFrom":[makeQuery(id+"F3.boolean.opBoolean","COPY",FACE,{"derivedFrom":makeQuery(id+"F3.opExtrude","SWEPT_FACE",FACE,{"disambiguationData":[OSD([subQ2])]})}),makeQuery(id+"F15.opExtrude","SWEPT_FACE",FACE,{"disambiguationData":[OSD([subQ0,subQ2])]})]})});}
            var sketch = newSketch(context, id + "F32", { "sketchPlane" : qUnion([Q0])});
            skLineSegment(sketch, "E40.bottom", {"start": v(-80.42, 7.86) * mm, "end": v(-8.35, 7.86) * mm});
            skLineSegment(sketch, "E40.top", {"start": v(-80.42, -8.1) * mm, "end": v(-8.35, -8.1) * mm});
            skLineSegment(sketch, "E40.left", {"start": v(-80.42, 7.86) * mm, "end": v(-80.42, -8.1) * mm});
            skLineSegment(sketch, "E40.right", {"start": v(-8.35, 7.86) * mm, "end": v(-8.35, -8.1) * mm});
            skSolve(sketch);
        }
        {
            var Q0;
            Q0=makeQuery(id+"F32.imprint","IMPRINT",FACE,{"disambiguationData":[TD([[makeQuery(id+"F32.imprint","IMPRINT",EDGE,{"derivedFrom":sQuery(id+"F32.wireOp",EDGE,"E40.bottom")}),-1.0]])]});
            var Q1;
            {var subQ0=sQuery(id+"F2.wireOp",EDGE,"E9");var subQ1=makeQuery(id+"F15.boolean.opBoolean","MERGE",FACE,{"derivedFrom":[makeQuery(id+"F3.boolean.opBoolean","COPY",FACE,{"derivedFrom":makeQuery(id+"F3.opExtrude","SWEPT_FACE",FACE,{"disambiguationData":[OSD([subQ0])]})}),makeQuery(id+"F15.opExtrude","SWEPT_FACE",FACE,{"disambiguationData":[OSD([sQuery(id+"F0.wireOp",EDGE,"E1.top"),subQ0])]})]});Q1=makeQuery(id+"F32.imprint","IMPRINT",FACE,{"disambiguationData":[TD([[makeQuery(id+"F32.imprint","IMPRINT",EDGE,{"derivedFrom":makeQuery(id+"F16.boolean.opBoolean","INTERSECT",EDGE,{"derivedFrom":[subQ1,makeQuery(id+"F16.opExtrude","SWEPT_FACE",FACE,{"disambiguationData":[OSD([sQuery(id+"F0.wireOp",EDGE,"E7.bottom")])]})]})}),-1.0]])]});}
            extrude(context, id + "F33", {"entities" : qUnion([Q0, Q1]), "operationType" : NewBodyOperationType.ADD, "oppositeDirection" : true, "depth" : 1 * mm});
        }
        {
            var Q0;
            {var subQ1=sQuery(id+"F2.wireOp",EDGE,"E10");var subQ2=sQuery(id+"F0.wireOp",EDGE,"E1.top");var subQ3=makeQuery(id+"F15.opExtrude","SWEPT_FACE",FACE,{"disambiguationData":[OSD([subQ2,subQ1])]});var subQ4=makeQuery(id+"F3.opExtrude","SWEPT_FACE",FACE,{"disambiguationData":[OSD([subQ1])]});var subQ5=makeQuery(id+"F3.boolean.opBoolean","COPY",FACE,{"derivedFrom":subQ4});var subQ6=makeQuery(id+"F15.boolean.opBoolean","MERGE",FACE,{"derivedFrom":[subQ5,subQ3]});var subQ9=makeQuery(id+"F16.opExtrude","SWEPT_FACE",FACE,{"disambiguationData":[OSD([sQuery(id+"F0.wireOp",EDGE,"E6.bottom")])]});Q0=makeQuery(id+"F21.imprint","IMPRINT",FACE,{"disambiguationData":[TD([[makeQuery(id+"F21.imprint","IMPRINT",EDGE,{"derivedFrom":makeQuery(id+"F16.boolean.opBoolean","INTERSECT",EDGE,{"derivedFrom":[subQ6,subQ9]})}),1.0]])]});}
            var sketch = newSketch(context, id + "F34", { "sketchPlane" : qUnion([Q0])});
            skLineSegment(sketch, "E41.bottom", {"start": v(8.73, 7.98) * mm, "end": v(80.6, 7.98) * mm});
            skLineSegment(sketch, "E41.top", {"start": v(8.73, -7.88) * mm, "end": v(80.6, -7.88) * mm});
            skLineSegment(sketch, "E41.left", {"start": v(8.73, 7.98) * mm, "end": v(8.73, -7.88) * mm});
            skLineSegment(sketch, "E41.right", {"start": v(80.6, 7.98) * mm, "end": v(80.6, -7.88) * mm});
            skSolve(sketch);
        }
        {
            var Q0;
            Q0=makeQuery(id+"F34.imprint","IMPRINT",FACE,{"disambiguationData":[TD([[makeQuery(id+"F34.imprint","IMPRINT",EDGE,{"derivedFrom":sQuery(id+"F34.wireOp",EDGE,"E41.bottom")}),-1.0]])]});
            var Q1;
            {var subQ0=sQuery(id+"F2.wireOp",EDGE,"E10");var subQ1=makeQuery(id+"F15.boolean.opBoolean","MERGE",FACE,{"derivedFrom":[makeQuery(id+"F3.boolean.opBoolean","COPY",FACE,{"derivedFrom":makeQuery(id+"F3.opExtrude","SWEPT_FACE",FACE,{"disambiguationData":[OSD([subQ0])]})}),makeQuery(id+"F15.opExtrude","SWEPT_FACE",FACE,{"disambiguationData":[OSD([sQuery(id+"F0.wireOp",EDGE,"E1.top"),subQ0])]})]});Q1=makeQuery(id+"F21.imprint","IMPRINT",FACE,{"disambiguationData":[TD([[makeQuery(id+"F21.imprint","IMPRINT",EDGE,{"derivedFrom":makeQuery(id+"F16.boolean.opBoolean","INTERSECT",EDGE,{"derivedFrom":[subQ1,makeQuery(id+"F16.opExtrude","SWEPT_FACE",FACE,{"disambiguationData":[OSD([sQuery(id+"F0.wireOp",EDGE,"E6.bottom")])]})]})}),-1.0]])]});}
            extrude(context, id + "F35", {"entities" : qUnion([Q0, Q1]), "operationType" : NewBodyOperationType.ADD, "oppositeDirection" : true, "depth" : 1 * mm});
        }
        {
            var Q0;
            {var subQ0=sQuery(id+"F0.wireOp",EDGE,"E1.top");var subQ2=sQuery(id+"F2.wireOp",EDGE,"E9");Q0=makeQuery(id+"F33.boolean.opBoolean","MERGE",FACE,{"derivedFrom":[makeQuery(id+"F17.boolean.opBoolean","SPLIT",FACE,{"disambiguationData":[TD([makeQuery(id+"F1.opExtrude","SWEPT_FACE",FACE,{"disambiguationData":[OSD([sQuery(id+"F0.wireOp",EDGE,"E1.bottom")])]})])],"derivedFrom":makeQuery(id+"F15.boolean.opBoolean","MERGE",FACE,{"derivedFrom":[makeQuery(id+"F3.boolean.opBoolean","COPY",FACE,{"derivedFrom":makeQuery(id+"F3.opExtrude","SWEPT_FACE",FACE,{"disambiguationData":[OSD([subQ2])]})}),makeQuery(id+"F15.opExtrude","SWEPT_FACE",FACE,{"disambiguationData":[OSD([subQ0,subQ2])]})]})}),makeQuery(id+"F33.opExtrude","CAP_FACE",FACE,{"disambiguationData":[OSD([sQuery(id+"F32.wireOp",EDGE,"E40.bottom"),sQuery(id+"F32.wireOp",EDGE,"E40.top"),sQuery(id+"F32.wireOp",EDGE,"E40.left"),sQuery(id+"F32.wireOp",EDGE,"E40.right")])],"isStart":true})]});}
            var sketch = newSketch(context, id + "F36", { "sketchPlane" : qUnion([Q0])});
            skText(sketch, "E42", { "text": "www.simtrack.com.au", "fontName": "OpenSans-Regular.ttf"});
            skLineSegment(sketch, "E43", {"start": v(-59.66, 1.4) * mm, "end": v(-59.66, 9) * mm});
            skLineSegment(sketch, "E44", {"start": v(-63.79, -1.4) * mm, "end": v(-63.79, -9) * mm});
            const initialGuessF36  = {"E42": [-0.08379, -0.0014, 1, 0, 0.0028]};
            skSetInitialGuess(sketch, initialGuessF36);
            skSolve(sketch);
        }
        {
            var Q0;
            Q0 = qSketchRegion(id + "F36", true);
            extrude(context, id + "F37", {"entities" : qUnion([Q0]), "operationType" : NewBodyOperationType.REMOVE, "oppositeDirection" : true, "depth" : .25 * mm});
        }
        {
            var Q0;
            {var subQ0=sQuery(id+"F2.wireOp",EDGE,"E10");var subQ1=sQuery(id+"F0.wireOp",EDGE,"E6.right");var subQ2=sQuery(id+"F0.wireOp",EDGE,"E6.left");var subQ3=sQuery(id+"F0.wireOp",EDGE,"E6.top");var subQ4=sQuery(id+"F0.wireOp",EDGE,"E6.bottom");var subQ5=sQuery(id+"F0.wireOp",EDGE,"E1.top");Q0=makeQuery(id+"F35.boolean.opBoolean","MERGE",FACE,{"derivedFrom":[makeQuery(id+"F17.boolean.opBoolean","SPLIT",FACE,{"disambiguationData":[TD([makeQuery(id+"F1.opExtrude","SWEPT_FACE",FACE,{"disambiguationData":[OSD([sQuery(id+"F0.wireOp",EDGE,"E1.bottom")])]})])],"derivedFrom":makeQuery(id+"F15.boolean.opBoolean","MERGE",FACE,{"derivedFrom":[makeQuery(id+"F3.boolean.opBoolean","COPY",FACE,{"derivedFrom":makeQuery(id+"F3.opExtrude","SWEPT_FACE",FACE,{"disambiguationData":[OSD([subQ0])]})}),makeQuery(id+"F15.opExtrude","SWEPT_FACE",FACE,{"disambiguationData":[OSD([subQ5,subQ0])]})]})}),makeQuery(id+"F35.opExtrude","CAP_FACE",FACE,{"disambiguationData":[OSD([subQ5,subQ4,subQ3,subQ2,subQ1,subQ0])],"isStart":true}),makeQuery(id+"F35.opExtrude","CAP_FACE",FACE,{"disambiguationData":[OSD([subQ5,subQ4,subQ3,subQ2,subQ1,subQ0,sQuery(id+"F34.wireOp",EDGE,"E41.bottom"),sQuery(id+"F34.wireOp",EDGE,"E41.top"),sQuery(id+"F34.wireOp",EDGE,"E41.left"),sQuery(id+"F34.wireOp",EDGE,"E41.right")])],"isStart":true})]});}
            var sketch = newSketch(context, id + "F38", { "sketchPlane" : qUnion([Q0])});
            skText(sketch, "E45", { "text": "made in Australia", "fontName": "OpenSans-Regular.ttf"});
            skLineSegment(sketch, "E46", {"start": v(58.79, 1.33) * mm, "end": v(58.79, 9) * mm});
            skLineSegment(sketch, "E47", {"start": v(58.79, -1.33) * mm, "end": v(58.79, -9) * mm});
            const initialGuessF38  = {"E45": [0.04379, -0.00133, 1, 0, 0.00266]};
            skSetInitialGuess(sketch, initialGuessF38);
            skSolve(sketch);
        }
        {
            var Q0;
            Q0 = qSketchRegion(id + "F38", true);
            extrude(context, id + "F39", {"entities" : qUnion([Q0]), "operationType" : NewBodyOperationType.REMOVE, "oppositeDirection" : true, "depth" : .25 * mm});
        }
        {
            var Q0;
            Q0=makeQuery(id+"F17.opExtrude","CAP_FACE",FACE,{"disambiguationData":[OSD([sQuery(id+"F0.wireOp",EDGE,"E0"),sQuery(id+"F0.wireOp",EDGE,"E8")])],"isStart":false});
            var sketch = newSketch(context, id + "F40", { "sketchPlane" : qUnion([Q0])});
            skCircle(sketch, "E48", {"center": v(0, 0) * mm, "radius": 6 * mm});
            skSolve(sketch);
        }
        {
            var Q0;
            Q0=makeQuery(id+"F40.imprint","IMPRINT",FACE,{"disambiguationData":[TD([[makeQuery(id+"F40.imprint","IMPRINT",EDGE,{"derivedFrom":sQuery(id+"F40.wireOp",EDGE,"E48")}),1.0]])]});
            extrude(context, id + "F41", {"entities" : qUnion([Q0]), "operationType" : NewBodyOperationType.REMOVE, "oppositeDirection" : true, "depth" : 1.5 * mm, "offsetDistance" : 25 * mm});
        }
        {
            var Q0;
            Q0=makeQuery(id+"F8.boolean.opBoolean","COPY",EDGE,{"derivedFrom":makeQuery(id+"F8.opExtrude","SWEPT_EDGE",EDGE,{"disambiguationData":[OSD([sQuery(id+"F7.wireOp",EDGE,"E16"),sQuery(id+"F7.wireOp",EDGE,"E17"),sQuery(id+"F7.wireOp",EDGE,"E20")])]})});
            var Q1;
            Q1=makeQuery(id+"F8.boolean.opBoolean","COPY",EDGE,{"derivedFrom":makeQuery(id+"F8.opExtrude","SWEPT_EDGE",EDGE,{"disambiguationData":[OSD([sQuery(id+"F7.wireOp",EDGE,"E11"),sQuery(id+"F7.wireOp",EDGE,"E12"),sQuery(id+"F7.wireOp",EDGE,"E15")])]})});
            var Q2;
            Q2=makeQuery(id+"F27.boolean.opBoolean","INTERSECT",EDGE,{"derivedFrom":[makeQuery(id+"F8.boolean.opBoolean","COPY",FACE,{"derivedFrom":makeQuery(id+"F8.opExtrude","SWEPT_FACE",FACE,{"disambiguationData":[OSD([sQuery(id+"F7.wireOp",EDGE,"E14")])]})}),makeQuery(id+"F27.opExtrude","SWEPT_FACE",FACE,{"disambiguationData":[OSD([sQuery(id+"F26.wireOp",EDGE,"E34.top")])]})]});
            var Q3;
            Q3=makeQuery(id+"F27.boolean.opBoolean","INTERSECT",EDGE,{"derivedFrom":[makeQuery(id+"F8.boolean.opBoolean","COPY",FACE,{"derivedFrom":makeQuery(id+"F8.opExtrude","SWEPT_FACE",FACE,{"disambiguationData":[OSD([sQuery(id+"F7.wireOp",EDGE,"E19")])]})}),makeQuery(id+"F27.opExtrude","SWEPT_FACE",FACE,{"disambiguationData":[OSD([sQuery(id+"F26.wireOp",EDGE,"E34.top")])]})]});
            chamfer(context, id + "F42", {"entities" : qUnion([Q0, Q1, Q2, Q3]), "width" : .7 * mm, "tangentPropagation" : true});
        }
        {
            var Q0;
            Q0=qCreatedBy(makeId("Front.planeOp"),FACE);
            var sketch = newSketch(context, id + "F43", { "sketchPlane" : qUnion([Q0])});
            skLineSegment(sketch, "E49.bottom", {"start": v(84.3, -4.5) * mm, "end": v(74.3, -4.5) * mm});
            skLineSegment(sketch, "E49.top", {"start": v(82.3, 1) * mm, "end": v(74.3, 1) * mm});
            skLineSegment(sketch, "E49.left", {"start": v(84.3, -4.5) * mm, "end": v(84.3, -1) * mm});
            skLineSegment(sketch, "E49.right", {"start": v(74.3, -4.5) * mm, "end": v(74.3, 1) * mm});
            skPoint(sketch, "E50.visualSharp", {"position": v(84.3, 1) * mm});
            skArc(sketch, "E50.filletArc", {"start": v(84.3, -1) * mm, "mid": v(83.71, 0.41) * mm, "end": v(82.3, 1) * mm});
            skLineSegment(sketch, "E51.MirrorCS", {"start": v(-74.3, -4.5) * mm, "end": v(-74.3, 1) * mm});
            skLineSegment(sketch, "E52.MirrorCS", {"start": v(-82.3, 1) * mm, "end": v(-74.3, 1) * mm});
            skArc(sketch, "E53.MirrorCS", {"start": v(-84.3, -1) * mm, "mid": v(-83.71, 0.41) * mm, "end": v(-82.3, 1) * mm});
            skLineSegment(sketch, "E54.MirrorCS", {"start": v(-84.3, -4.5) * mm, "end": v(-84.3, -1) * mm});
            skLineSegment(sketch, "E55.MirrorCS", {"start": v(-84.3, -4.5) * mm, "end": v(-74.3, -4.5) * mm});
            skSolve(sketch);
        }
        {
            var Q0;
            Q0 = qSketchRegion(id + "F43", true);
            extrude(context, id + "F44", {"entities" : qUnion([Q0]), "operationType" : NewBodyOperationType.ADD, "depth" : 12.5 * mm, "offsetDistance" : 25 * mm, "hasSecondDirection" : true, "secondDirectionOppositeDirection" : true, "secondDirectionDepth" : 12.5 * mm});
        }
    });
